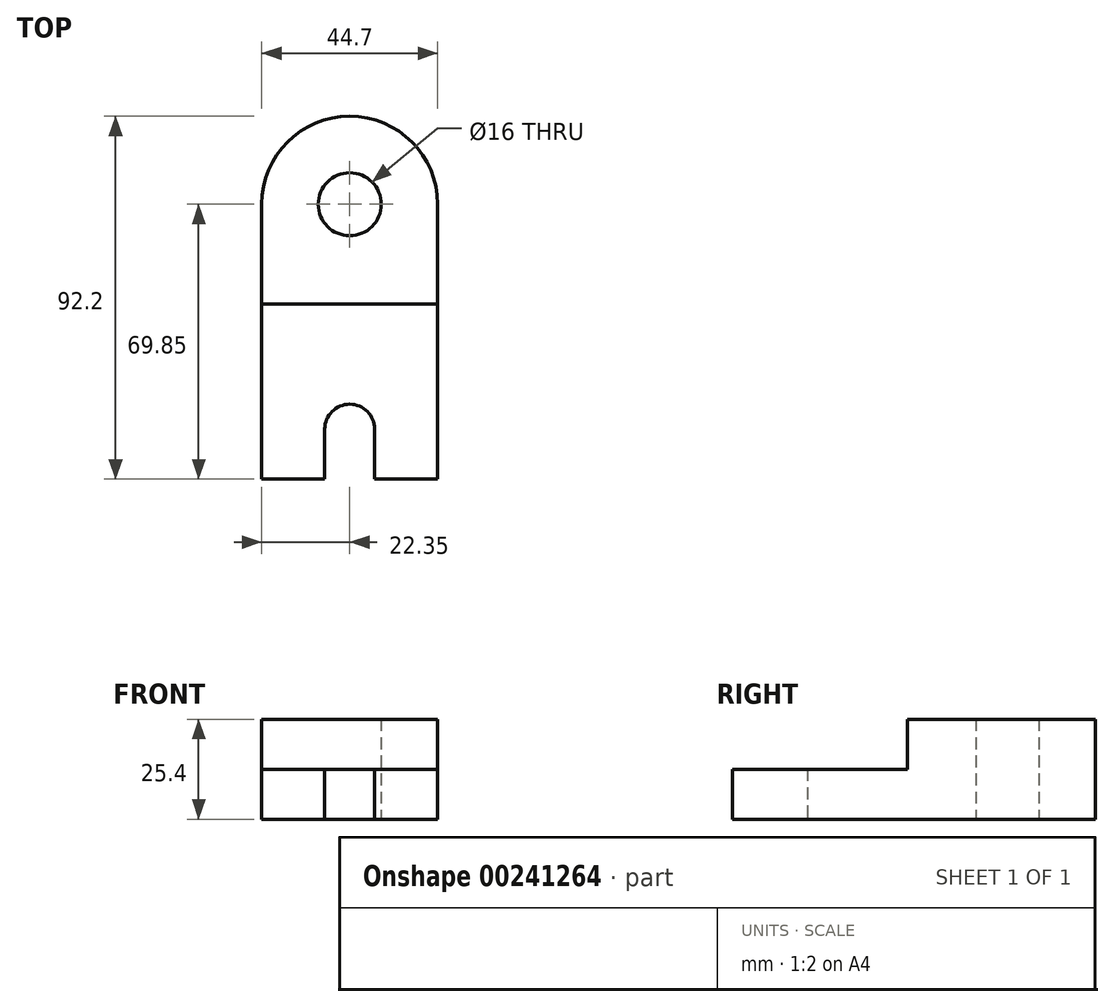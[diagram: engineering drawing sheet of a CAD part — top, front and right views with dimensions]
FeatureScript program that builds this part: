
annotation { "Feature Type Name" : "Feature", "Feature Type Description" : "" }
export const myFeature = defineFeature(function(context is Context, id is Id, definition is map)
    precondition{}
    {
        {
            var Q0;
            Q0=qCreatedBy(makeId("Top.planeOp"),FACE);
            var sketch = newSketch(context, id + "F0", { "sketchPlane" : qUnion([Q0])});
            skLineSegment(sketch, "E0", {"start": v(0, 0) * mm, "end": v(-16, 0) * mm});
            skLineSegment(sketch, "E1", {"start": v(-16, 0) * mm, "end": v(-16, 44.45) * mm});
            skLineSegment(sketch, "E2", {"start": v(28.7, 44.45) * mm, "end": v(28.7, 0) * mm});
            skLineSegment(sketch, "E3", {"start": v(28.7, 0) * mm, "end": v(12.7, 0) * mm});
            skLineSegment(sketch, "E4", {"start": v(12.7, 0) * mm, "end": v(12.7, 12.7) * mm});
            skArc(sketch, "E5", {"start": v(12.7, 12.7) * mm, "mid": v(6.35, 19.05) * mm, "end": v(0, 12.7) * mm});
            skLineSegment(sketch, "E6", {"start": v(0, 0) * mm, "end": v(0, 12.7) * mm});
            skLineSegment(sketch, "E7", {"start": v(-16, 44.45) * mm, "end": v(-16, 69.85) * mm});
            skLineSegment(sketch, "E8", {"start": v(28.7, 44.45) * mm, "end": v(28.7, 69.85) * mm});
            skArc(sketch, "E9", {"start": v(28.7, 69.85) * mm, "mid": v(6.35, 92.2) * mm, "end": v(-16, 69.85) * mm});
            skCircle(sketch, "E10", {"center": v(6.35, 69.85) * mm, "radius": 8 * mm});
            skSolve(sketch);
        }
        {
            var Q0;
            Q0=makeQuery(id+"F0.imprint","IMPRINT",FACE,{"disambiguationData":[TD([[makeQuery(id+"F0.imprint","IMPRINT",EDGE,{"derivedFrom":sQuery(id+"F0.wireOp",EDGE,"E0")}),-1.0]])]});
            extrude(context, id + "F1", {"entities" : qUnion([Q0]), "depth" : 12.7 * mm});
        }
        {
            var Q0;
            Q0=makeQuery(id+"F1.opExtrude","CAP_FACE",FACE,{"disambiguationData":[OSD([sQuery(id+"F0.wireOp",EDGE,"E0"),sQuery(id+"F0.wireOp",EDGE,"E1"),sQuery(id+"F0.wireOp",EDGE,"E2"),sQuery(id+"F0.wireOp",EDGE,"E3"),sQuery(id+"F0.wireOp",EDGE,"E4"),sQuery(id+"F0.wireOp",EDGE,"E5"),sQuery(id+"F0.wireOp",EDGE,"E6"),sQuery(id+"F0.wireOp",EDGE,"E7"),sQuery(id+"F0.wireOp",EDGE,"E8"),sQuery(id+"F0.wireOp",EDGE,"E9")])],"isStart":false});
            var sketch = newSketch(context, id + "F2", { "sketchPlane" : qUnion([Q0])});
            skLineSegment(sketch, "E11", {"start": v(-16, 0) * mm, "end": v(-16, 44.45) * mm});
            skLineSegment(sketch, "E12", {"start": v(-16, 44.45) * mm, "end": v(28.7, 44.45) * mm});
            skSolve(sketch);
        }
        {
            var Q0;
            {var subQ0=sQuery(id+"F2.wireOp",EDGE,"E12");Q0=makeQuery(id+"F2.imprint","IMPRINT",FACE,{"disambiguationData":[TD([[makeQuery(id+"F2.imprint","IMPRINT",EDGE,{"derivedFrom":subQ0}),1.0]])]});}
            extrude(context, id + "F3", {"entities" : qUnion([Q0]), "operationType" : NewBodyOperationType.ADD, "depth" : 12.7 * mm});
        }
    });
